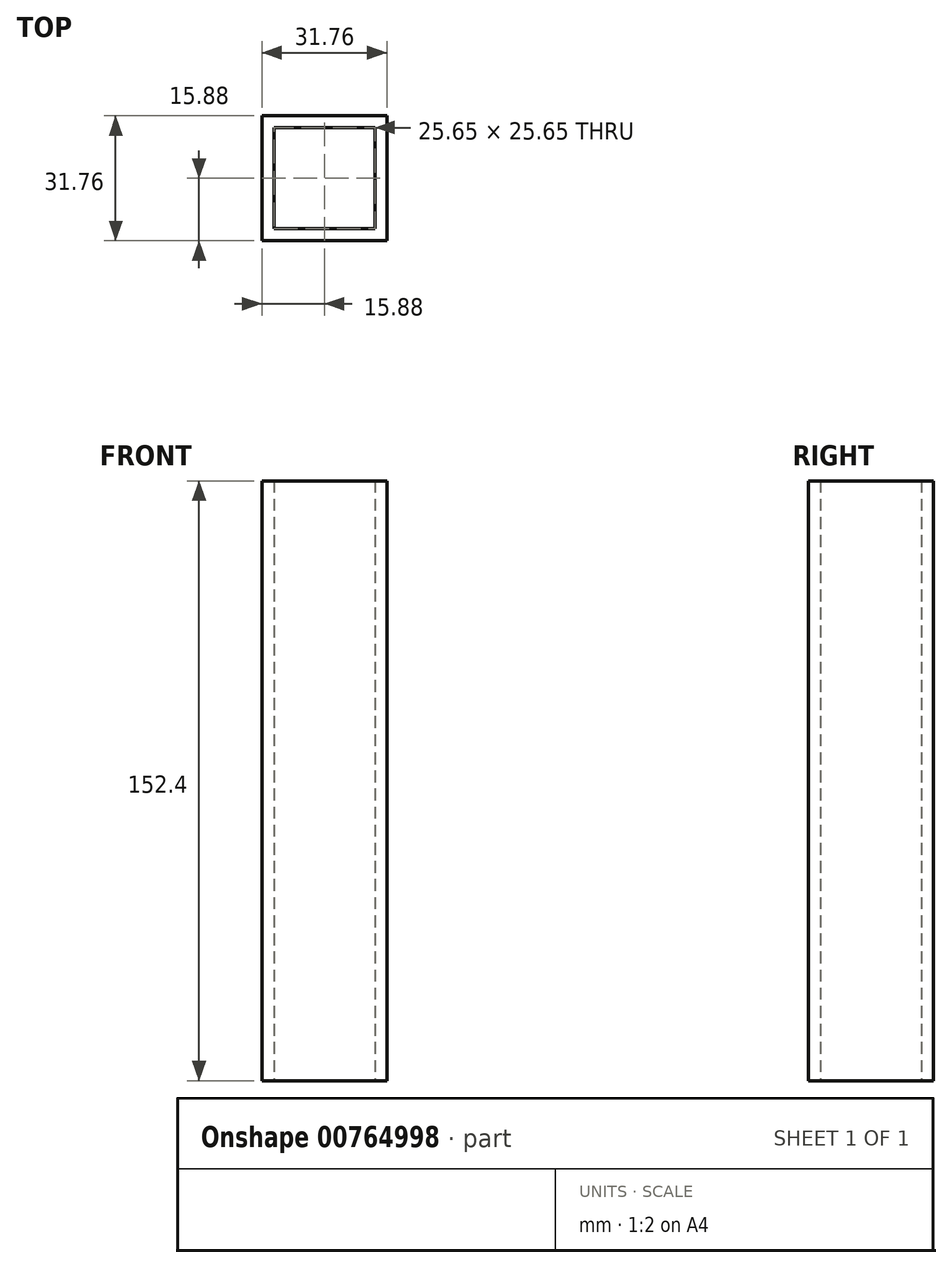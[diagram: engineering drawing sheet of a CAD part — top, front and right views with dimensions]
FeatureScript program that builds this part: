
annotation { "Feature Type Name" : "Feature", "Feature Type Description" : "" }
export const myFeature = defineFeature(function(context is Context, id is Id, definition is map)
    precondition{}
    {
        {
            var Q0;
            Q0=qCreatedBy(makeId("Top.planeOp"),FACE);
            var sketch = newSketch(context, id + "F0", { "sketchPlane" : qUnion([Q0])});
            skLineSegment(sketch, "E0.bottom", {"start": v(15.88, 15.88) * mm, "end": v(-15.88, 15.88) * mm});
            skLineSegment(sketch, "E0.top", {"start": v(15.88, -15.88) * mm, "end": v(-15.88, -15.88) * mm});
            skLineSegment(sketch, "E0.left", {"start": v(15.88, 15.88) * mm, "end": v(15.88, -15.88) * mm});
            skLineSegment(sketch, "E0.right", {"start": v(-15.88, 15.87) * mm, "end": v(-15.88, -15.88) * mm});
            skPoint(sketch, "E0.middle", {"position": v(0, 0) * mm});
            skLineSegment(sketch, "E1.0", {"start": v(12.83, -12.83) * mm, "end": v(-12.83, -12.83) * mm});
            skLineSegment(sketch, "E1.1", {"start": v(12.83, 12.83) * mm, "end": v(12.83, -12.83) * mm});
            skLineSegment(sketch, "E1.2", {"start": v(12.83, 12.83) * mm, "end": v(-12.83, 12.83) * mm});
            skLineSegment(sketch, "E1.3", {"start": v(-12.83, 12.83) * mm, "end": v(-12.83, -12.83) * mm});
            skSolve(sketch);
        }
        {
            var Q0;
            Q0 = qSketchRegion(id + "F0", true);
            extrude(context, id + "F1", {"entities" : qUnion([Q0]), "depth" : 152.4 * mm, "offsetDistance" : 25.4 * mm});
        }
    });
